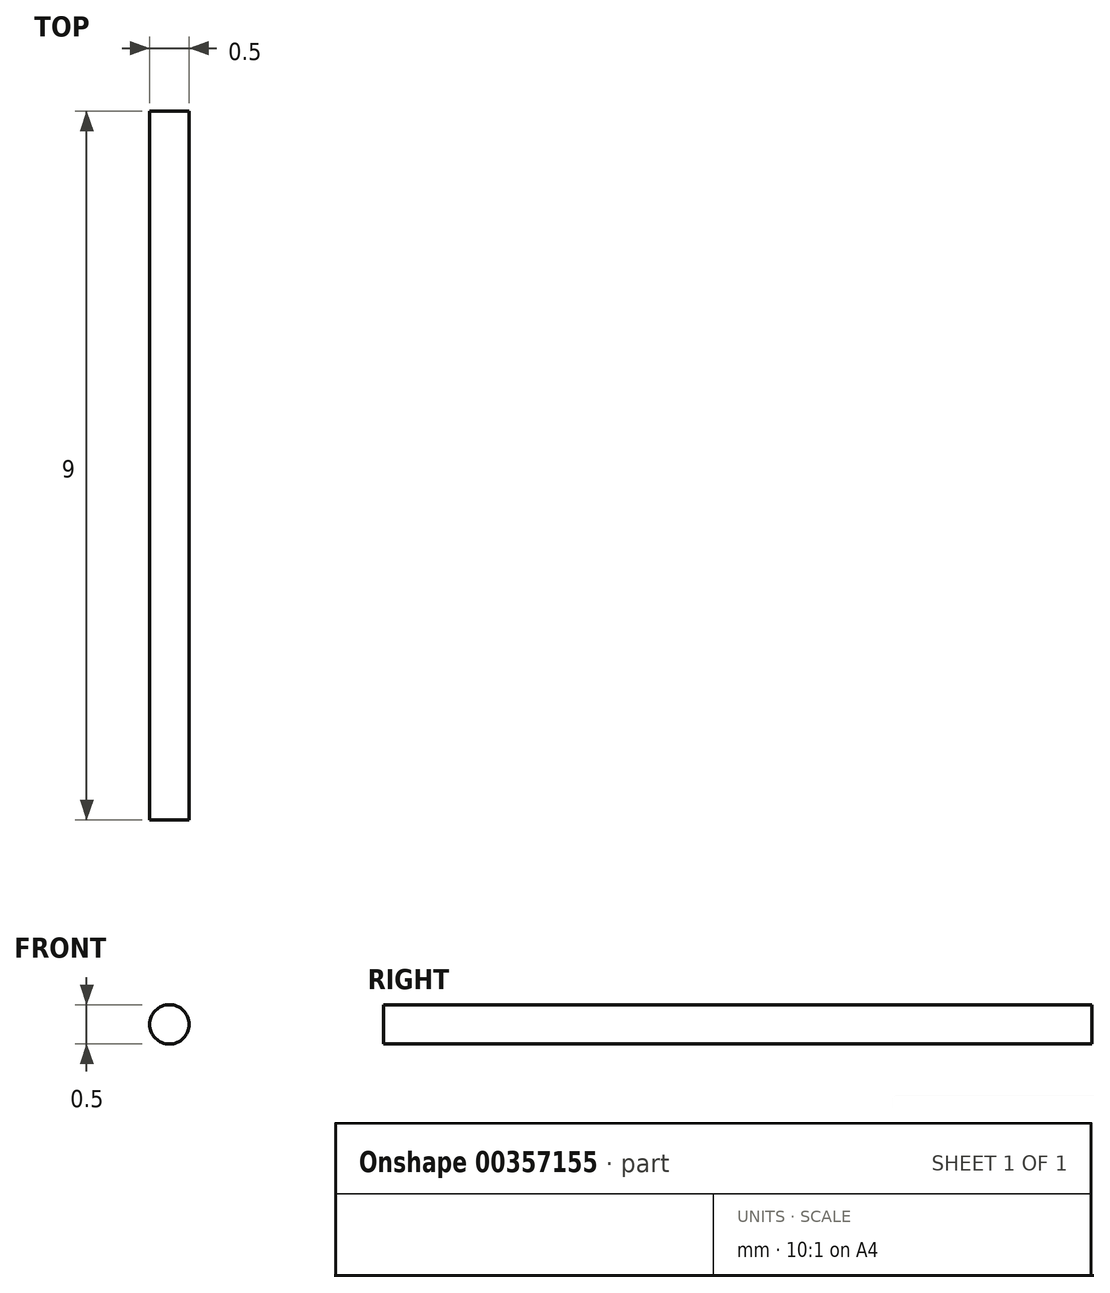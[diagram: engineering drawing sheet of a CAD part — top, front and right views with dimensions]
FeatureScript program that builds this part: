
annotation { "Feature Type Name" : "Feature", "Feature Type Description" : "" }
export const myFeature = defineFeature(function(context is Context, id is Id, definition is map)
    precondition{}
    {
        {
            var Q0;
            Q0=qCreatedBy(makeId("Front.planeOp"),FACE);
            var sketch = newSketch(context, id + "F0", { "sketchPlane" : qUnion([Q0])});
            skCircle(sketch, "E0", {"center": v(0, 0) * mm, "radius": 0.25 * mm});
            skSolve(sketch);
        }
        {
            var Q0;
            Q0 = qSketchRegion(id + "F0", true);
            extrude(context, id + "F1", {"entities" : qUnion([Q0]), "depth" : 9 * mm});
        }
    });
